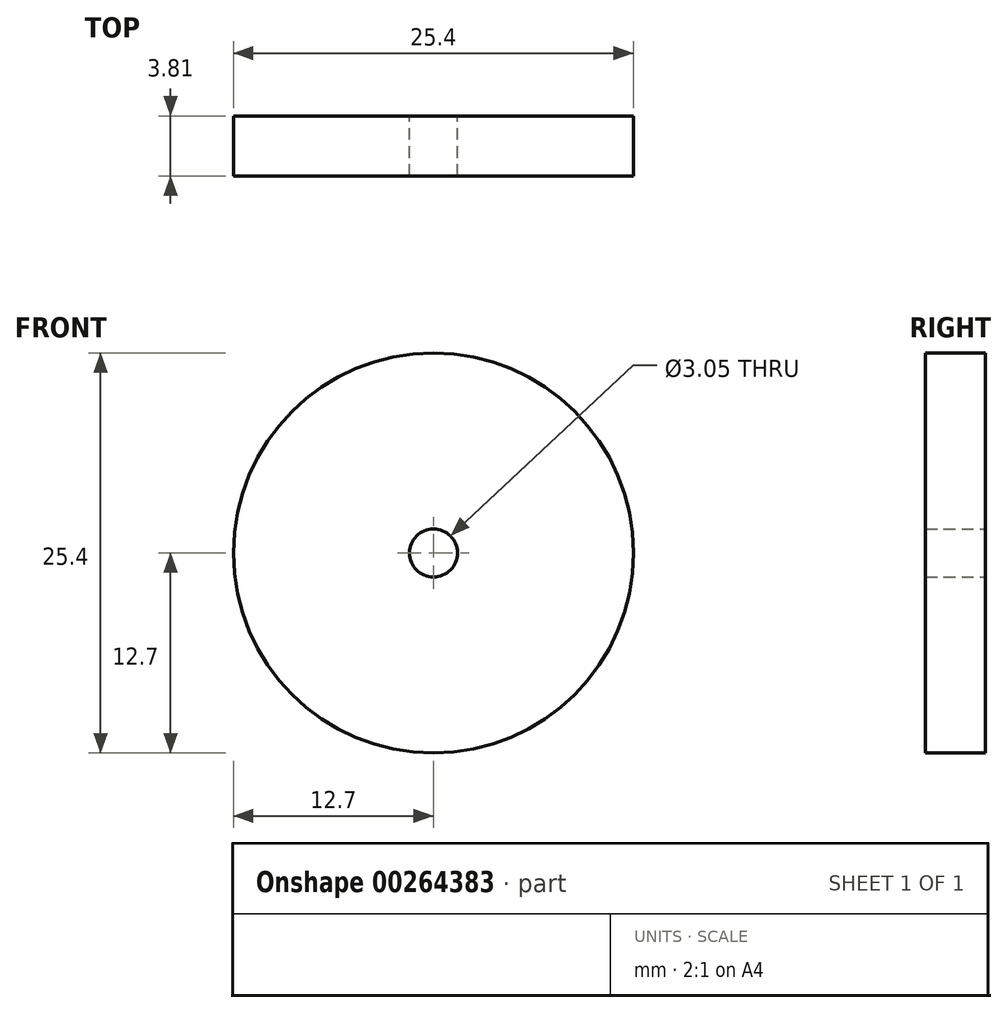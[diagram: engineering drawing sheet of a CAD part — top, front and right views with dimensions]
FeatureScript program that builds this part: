
annotation { "Feature Type Name" : "Feature", "Feature Type Description" : "" }
export const myFeature = defineFeature(function(context is Context, id is Id, definition is map)
    precondition{}
    {
        {
            var Q0;
            Q0=qCreatedBy(makeId("Front.planeOp"),FACE);
            var sketch = newSketch(context, id + "F0", { "sketchPlane" : qUnion([Q0])});
            skCircle(sketch, "E0", {"center": v(0, 0) * mm, "radius": 12.7 * mm});
            skCircle(sketch, "E1", {"center": v(0, 0) * mm, "radius": 1.52 * mm});
            skSolve(sketch);
        }
        {
            var Q0;
            Q0 = qSketchRegion(id + "F0", true);
            extrude(context, id + "F1", {"entities" : qUnion([Q0]), "depth" : 3.8 * mm});
        }
    });
